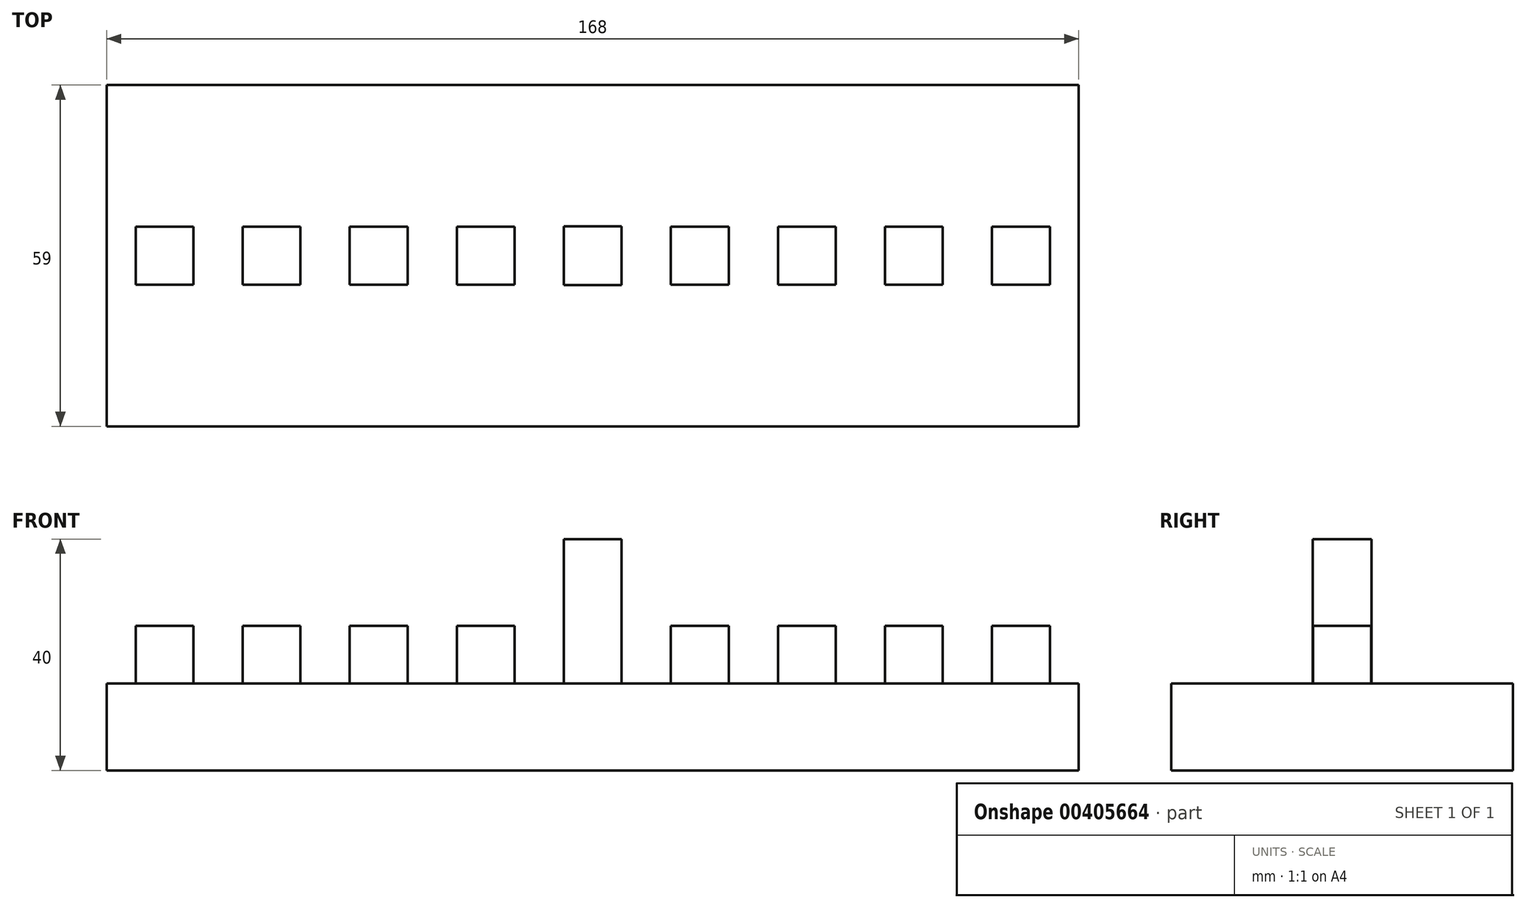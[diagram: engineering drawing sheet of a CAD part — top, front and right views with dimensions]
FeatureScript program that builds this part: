
annotation { "Feature Type Name" : "Feature", "Feature Type Description" : "" }
export const myFeature = defineFeature(function(context is Context, id is Id, definition is map)
    precondition{}
    {
        {
            var Q0;
            Q0=qCreatedBy(makeId("Top.planeOp"),FACE);
            var sketch = newSketch(context, id + "F0", { "sketchPlane" : qUnion([Q0])});
            skLineSegment(sketch, "E0.bottom", {"start": v(84, 29.5) * mm, "end": v(-84, 29.5) * mm});
            skLineSegment(sketch, "E0.top", {"start": v(84, -29.5) * mm, "end": v(-84, -29.5) * mm});
            skLineSegment(sketch, "E0.left", {"start": v(84, 29.5) * mm, "end": v(84, -29.5) * mm});
            skLineSegment(sketch, "E0.right", {"start": v(-84, 29.5) * mm, "end": v(-84, -29.5) * mm});
            skPoint(sketch, "E0.middle", {"position": v(0, 0) * mm});
            skSolve(sketch);
        }
        {
            var Q0;
            Q0=qCreatedBy(makeId("Top.planeOp"),FACE);
            var sketch = newSketch(context, id + "F1", { "sketchPlane" : qUnion([Q0])});
            skLineSegment(sketch, "E1.bottom", {"start": v(5, 5.08) * mm, "end": v(-5, 5.08) * mm});
            skLineSegment(sketch, "E1.top", {"start": v(5, -5.08) * mm, "end": v(-5, -5.08) * mm});
            skLineSegment(sketch, "E1.left", {"start": v(5, 5.08) * mm, "end": v(5, -5.08) * mm});
            skLineSegment(sketch, "E1.right", {"start": v(-5, 5.08) * mm, "end": v(-5, -5.08) * mm});
            skPoint(sketch, "E1.middle", {"position": v(0, 0) * mm});
            skSolve(sketch);
        }
        {
            var Q0;
            Q0 = qSketchRegion(id + "F0", true);
            extrude(context, id + "F2", {"entities" : qUnion([Q0]), "depth" : 15 * mm});
        }
        {
            var Q0;
            Q0=qCreatedBy(makeId("Top.planeOp"),FACE);
            var sketch = newSketch(context, id + "F3", { "sketchPlane" : qUnion([Q0])});
            skLineSegment(sketch, "E2.bottom", {"start": v(-69, 5) * mm, "end": v(-79, 5) * mm});
            skLineSegment(sketch, "E2.top", {"start": v(-69, -5) * mm, "end": v(-79, -5) * mm});
            skLineSegment(sketch, "E2.left", {"start": v(-69, 5) * mm, "end": v(-69, -5) * mm});
            skLineSegment(sketch, "E2.right", {"start": v(-79, 5) * mm, "end": v(-79, -5) * mm});
            skPoint(sketch, "E2.middle", {"position": v(-74, 0) * mm});
            skLineSegment(sketch, "E3.bottom", {"start": v(-50.5, 5) * mm, "end": v(-60.5, 5) * mm});
            skLineSegment(sketch, "E3.top", {"start": v(-50.5, -5) * mm, "end": v(-60.5, -5) * mm});
            skLineSegment(sketch, "E3.left", {"start": v(-50.5, 5) * mm, "end": v(-50.5, -5) * mm});
            skLineSegment(sketch, "E3.right", {"start": v(-60.5, 5) * mm, "end": v(-60.5, -5) * mm});
            skPoint(sketch, "E3.middle", {"position": v(-55.5, 0) * mm});
            skLineSegment(sketch, "E4.bottom", {"start": v(-32, 5) * mm, "end": v(-42, 5) * mm});
            skLineSegment(sketch, "E4.top", {"start": v(-32, -5) * mm, "end": v(-42, -5) * mm});
            skLineSegment(sketch, "E4.left", {"start": v(-32, 5) * mm, "end": v(-32, -5) * mm});
            skLineSegment(sketch, "E4.right", {"start": v(-42, 5) * mm, "end": v(-42, -5) * mm});
            skPoint(sketch, "E4.middle", {"position": v(-37, 0) * mm});
            skPoint(sketch, "E4.cornerSnap0", {"position": v(-74, 5) * mm});
            skLineSegment(sketch, "E5.bottom", {"start": v(-13.5, 5) * mm, "end": v(-23.5, 5) * mm});
            skLineSegment(sketch, "E5.top", {"start": v(-13.5, -5) * mm, "end": v(-23.5, -5) * mm});
            skLineSegment(sketch, "E5.left", {"start": v(-13.5, 5) * mm, "end": v(-13.5, -5) * mm});
            skLineSegment(sketch, "E5.right", {"start": v(-23.5, 5) * mm, "end": v(-23.5, -5) * mm});
            skPoint(sketch, "E5.middle", {"position": v(-18.5, 0) * mm});
            skLineSegment(sketch, "E6.MirrorCS", {"start": v(13.5, 5) * mm, "end": v(23.5, 5) * mm});
            skLineSegment(sketch, "E7.MirrorCS", {"start": v(13.5, 5) * mm, "end": v(13.5, -5) * mm});
            skLineSegment(sketch, "E8.MirrorCS", {"start": v(13.5, -5) * mm, "end": v(23.5, -5) * mm});
            skLineSegment(sketch, "E9.MirrorCS", {"start": v(23.5, 5) * mm, "end": v(23.5, -5) * mm});
            skLineSegment(sketch, "E10.MirrorCS", {"start": v(32, 5) * mm, "end": v(32, -5) * mm});
            skLineSegment(sketch, "E11.MirrorCS", {"start": v(32, 5) * mm, "end": v(42, 5) * mm});
            skLineSegment(sketch, "E12.MirrorCS", {"start": v(42, 5) * mm, "end": v(42, -5) * mm});
            skLineSegment(sketch, "E13.MirrorCS", {"start": v(32, -5) * mm, "end": v(42, -5) * mm});
            skLineSegment(sketch, "E14.MirrorCS", {"start": v(50.5, -5) * mm, "end": v(60.5, -5) * mm});
            skLineSegment(sketch, "E15.MirrorCS", {"start": v(50.5, 5) * mm, "end": v(50.5, -5) * mm});
            skLineSegment(sketch, "E16.MirrorCS", {"start": v(50.5, 5) * mm, "end": v(60.5, 5) * mm});
            skLineSegment(sketch, "E17.MirrorCS", {"start": v(60.5, 5) * mm, "end": v(60.5, -5) * mm});
            skLineSegment(sketch, "E18.MirrorCS", {"start": v(69, 5) * mm, "end": v(79, 5) * mm});
            skLineSegment(sketch, "E19.MirrorCS", {"start": v(69, 5) * mm, "end": v(69, -5) * mm});
            skLineSegment(sketch, "E20.MirrorCS", {"start": v(69, -5) * mm, "end": v(79, -5) * mm});
            skLineSegment(sketch, "E21.MirrorCS", {"start": v(79, 5) * mm, "end": v(79, -5) * mm});
            skSolve(sketch);
        }
        {
            var Q0;
            Q0 = qSketchRegion(id + "F3", true);
            extrude(context, id + "F4", {"entities" : qUnion([Q0]), "operationType" : NewBodyOperationType.ADD, "depth" : 25 * mm});
        }
        {
            var Q0;
            Q0 = qSketchRegion(id + "F1", true);
            extrude(context, id + "F5", {"entities" : qUnion([Q0]), "operationType" : NewBodyOperationType.ADD, "depth" : 40 * mm});
        }
    });
